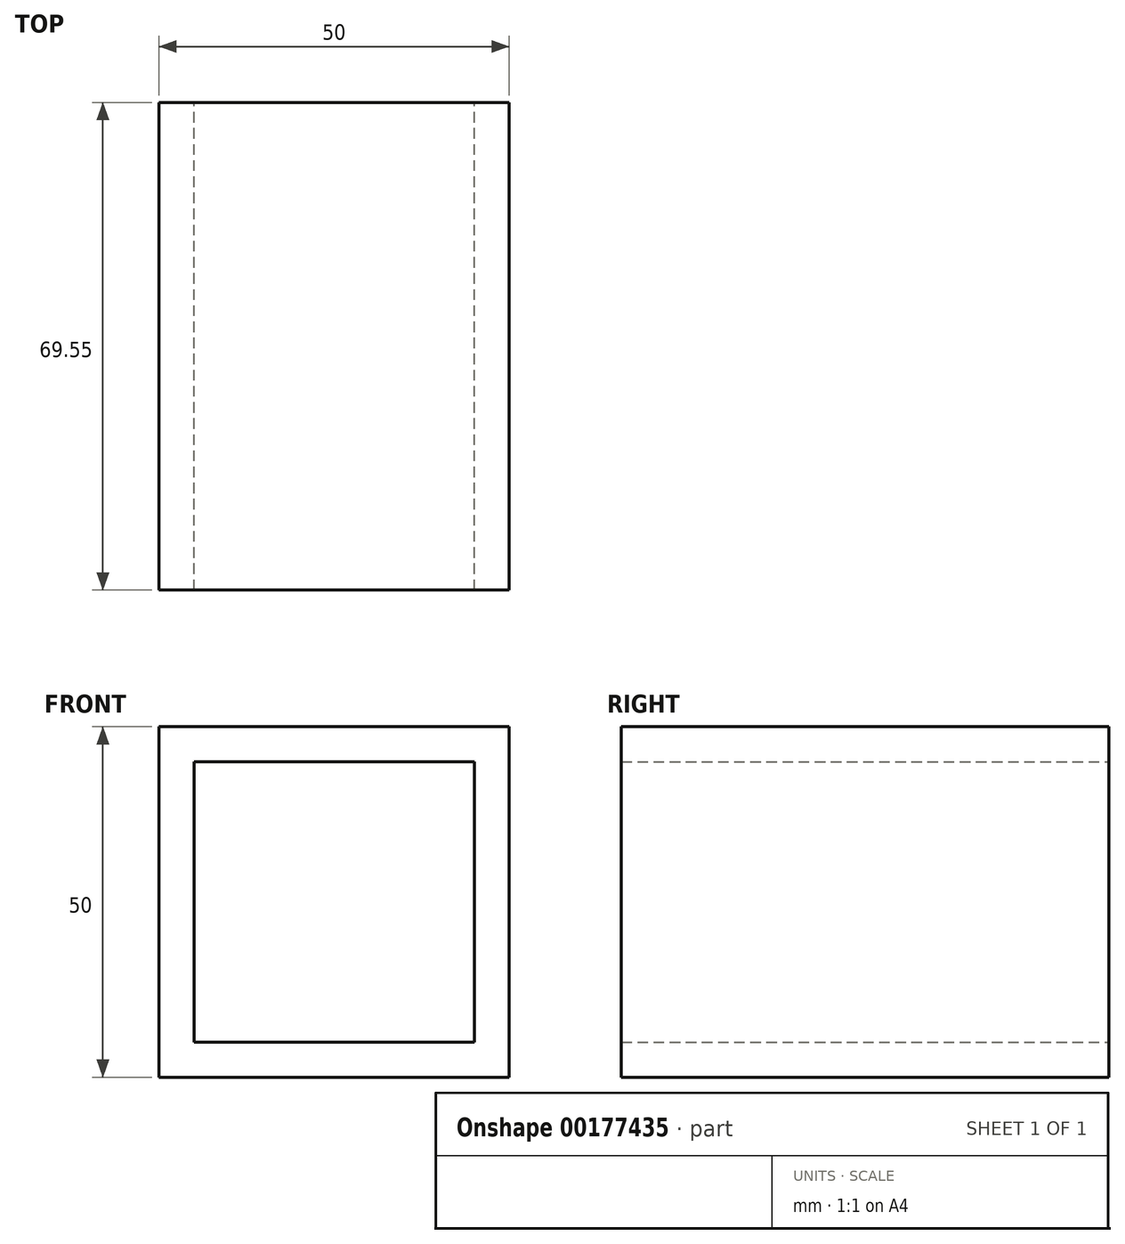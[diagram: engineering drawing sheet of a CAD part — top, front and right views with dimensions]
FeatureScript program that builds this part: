
annotation { "Feature Type Name" : "Feature", "Feature Type Description" : "" }
export const myFeature = defineFeature(function(context is Context, id is Id, definition is map)
    precondition{}
    {
        {
            var Q0;
            Q0=qCreatedBy(makeId("Front.planeOp"),FACE);
            var sketch = newSketch(context, id + "F0", { "sketchPlane" : qUnion([Q0])});
            skLineSegment(sketch, "E0.bottom", {"start": v(25, -25) * mm, "end": v(-25, -25) * mm});
            skLineSegment(sketch, "E0.top", {"start": v(25, 25) * mm, "end": v(-25, 25) * mm});
            skLineSegment(sketch, "E0.left", {"start": v(25, -25) * mm, "end": v(25, 25) * mm});
            skLineSegment(sketch, "E0.right", {"start": v(-25, -25) * mm, "end": v(-25, 25) * mm});
            skPoint(sketch, "E0.middle", {"position": v(0, 0) * mm});
            skLineSegment(sketch, "E1.0", {"start": v(20, 20) * mm, "end": v(-20, 20) * mm});
            skLineSegment(sketch, "E1.1", {"start": v(20, -20) * mm, "end": v(20, 20) * mm});
            skLineSegment(sketch, "E1.2", {"start": v(20, -20) * mm, "end": v(-20, -20) * mm});
            skLineSegment(sketch, "E1.3", {"start": v(-20, -20) * mm, "end": v(-20, 20) * mm});
            skSolve(sketch);
        }
        {
            var Q0;
            Q0=makeQuery(id+"F0.imprint","IMPRINT",FACE,{"disambiguationData":[TD([[makeQuery(id+"F0.imprint","IMPRINT",EDGE,{"derivedFrom":sQuery(id+"F0.wireOp",EDGE,"E0.bottom")}),-1.0]])]});
            extrude(context, id + "F1", {"entities" : qUnion([Q0]), "depth" : 69.55 * mm});
        }
    });
